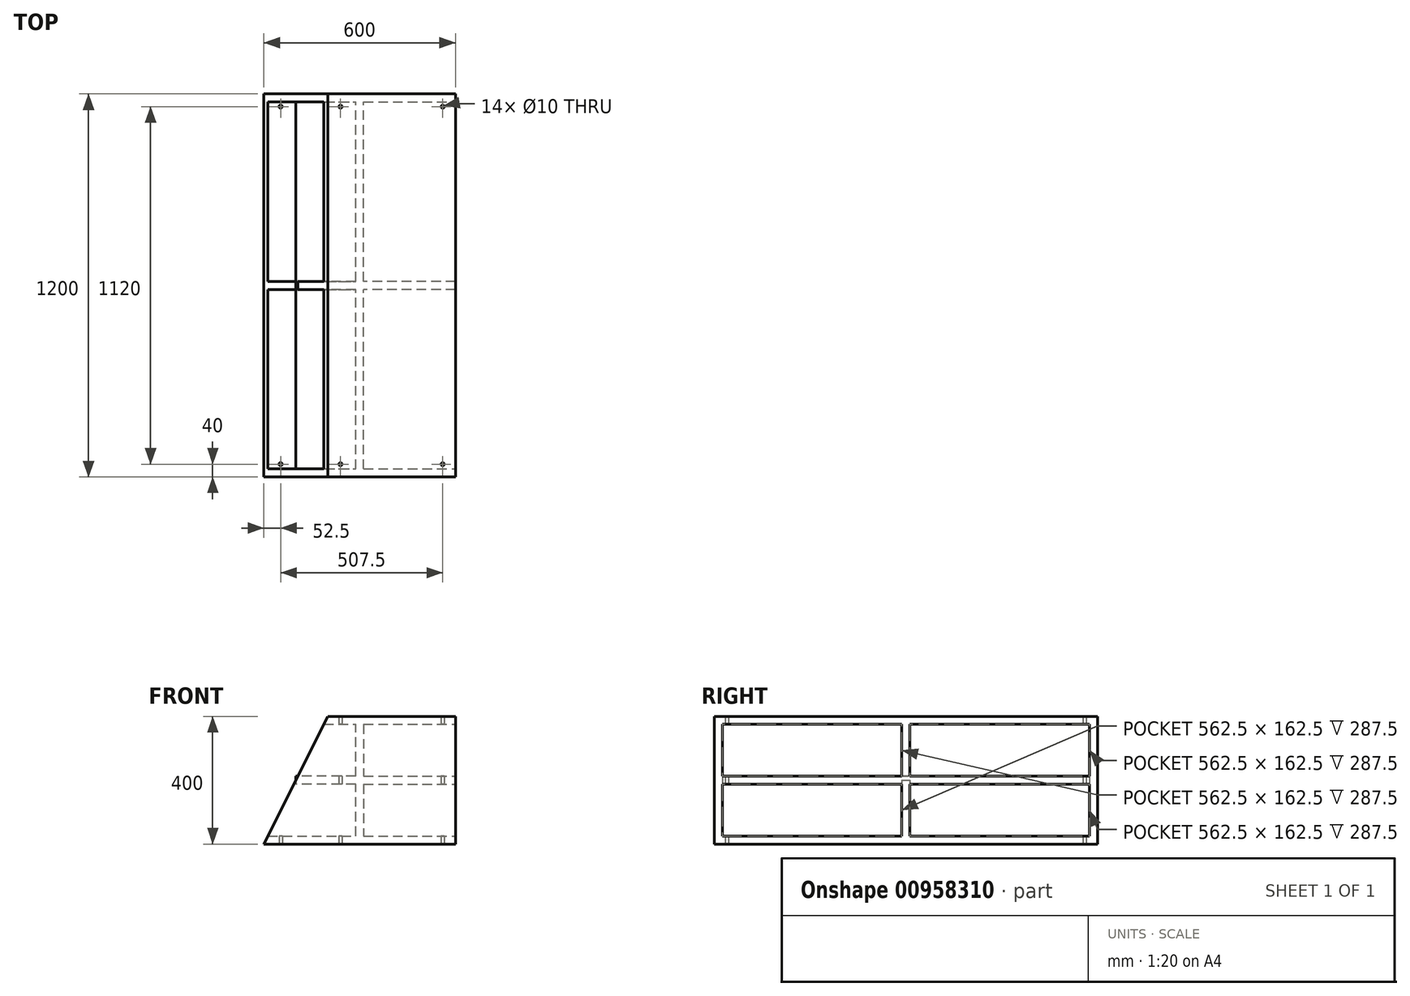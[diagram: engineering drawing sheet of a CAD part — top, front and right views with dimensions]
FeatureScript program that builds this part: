
annotation { "Feature Type Name" : "Feature", "Feature Type Description" : "" }
export const myFeature = defineFeature(function(context is Context, id is Id, definition is map)
    precondition{}
    {
        {
            var Q0;
            Q0=qCreatedBy(makeId("Front.planeOp"),FACE);
            var sketch = newSketch(context, id + "F0", { "sketchPlane" : qUnion([Q0])});
            skLineSegment(sketch, "E0.bottom", {"start": v(-400, 200) * mm, "end": v(0, 200) * mm});
            skLineSegment(sketch, "E0.top", {"start": v(-600, -200) * mm, "end": v(0, -200) * mm});
            skLineSegment(sketch, "E0.left", {"start": v(-400, 200) * mm, "end": v(-600, -200) * mm});
            skLineSegment(sketch, "E0.right", {"start": v(0, 200) * mm, "end": v(0, -200) * mm});
            skPoint(sketch, "E1", {"position": v(0, -200) * mm});
            skPoint(sketch, "E2", {"position": v(-500, 0) * mm});
            skSolve(sketch);
        }
        {
            var Q0;
            Q0=makeQuery(id+"F0.imprint","IMPRINT",FACE,{"disambiguationData":[TD([[makeQuery(id+"F0.imprint","IMPRINT",EDGE,{"derivedFrom":sQuery(id+"F0.wireOp",EDGE,"E0.bottom")}),-1.0]])]});
            extrude(context, id + "F1", {"entities" : qUnion([Q0]), "endBound" : BoundingType.SYMMETRIC, "depth" : 1200 * mm, "offsetDistance" : 25 * mm});
        }
        {
            var Q0;
            Q0=makeQuery(id+"F1.opExtrude","SWEPT_FACE",FACE,{"disambiguationData":[OSD([sQuery(id+"F0.wireOp",EDGE,"E0.right")])]});
            var Q1;
            Q1=makeQuery(id+"F1.opExtrude","SWEPT_FACE",FACE,{"disambiguationData":[OSD([sQuery(id+"F0.wireOp",EDGE,"E0.left")])]});
            shell(context, id + "F2", {"entities" : qUnion([Q0, Q1]), "thickness" : 25 * mm});
        }
        {
            var Q0;
            Q0=makeQuery(id+"F0.imprint","IMPRINT",FACE,{"disambiguationData":[TD([[makeQuery(id+"F0.imprint","IMPRINT",EDGE,{"derivedFrom":sQuery(id+"F0.wireOp",EDGE,"E0.bottom")}),-1.0]])]});
            extrude(context, id + "F3", {"entities" : qUnion([Q0]), "operationType" : NewBodyOperationType.ADD, "endBound" : BoundingType.SYMMETRIC, "depth" : 25 * mm, "offsetDistance" : 25 * mm});
        }
        {
            var Q0;
            Q0=qCreatedBy(makeId("Top.planeOp"),FACE);
            var sketch = newSketch(context, id + "F4", { "sketchPlane" : qUnion([Q0])});
            skLineSegment(sketch, "E3.bottom", {"start": v(-500, -575) * mm, "end": v(0, -575) * mm});
            skLineSegment(sketch, "E3.top", {"start": v(-500, 575) * mm, "end": v(0, 575) * mm});
            skLineSegment(sketch, "E3.left", {"start": v(-500, -575) * mm, "end": v(-500, 575) * mm});
            skLineSegment(sketch, "E3.right", {"start": v(0, -575) * mm, "end": v(0, 575) * mm});
            skSolve(sketch);
        }
        {
            var Q0;
            Q0 = qSketchRegion(id + "F4", true);
            extrude(context, id + "F5", {"entities" : qUnion([Q0]), "operationType" : NewBodyOperationType.ADD, "endBound" : BoundingType.SYMMETRIC, "depth" : 25 * mm, "offsetDistance" : 25 * mm});
        }
        {
            var Q0;
            Q0=qCreatedBy(makeId("Right.planeOp"),FACE);
            cPlane(context, id + "F6", {"entities" : qUnion([Q0]), "cplaneType" : CPlaneType.OFFSET, "offset" : 300 * mm, "oppositeDirection" : true, "width" : 150 * mm, "height" : 150 * mm});
        }
        {
            var Q0;
            Q0=qCreatedBy(id+"F6.planeOp",FACE);
            var sketch = newSketch(context, id + "F7", { "sketchPlane" : qUnion([Q0])});
            skLineSegment(sketch, "E4.bottom", {"start": v(-575, 175) * mm, "end": v(575, 175) * mm});
            skLineSegment(sketch, "E4.top", {"start": v(-575, -175) * mm, "end": v(575, -175) * mm});
            skLineSegment(sketch, "E4.left", {"start": v(-575, 175) * mm, "end": v(-575, -175) * mm});
            skLineSegment(sketch, "E4.right", {"start": v(575, 175) * mm, "end": v(575, -175) * mm});
            skSolve(sketch);
        }
        {
            var Q0;
            Q0=makeQuery(id+"F7.imprint","IMPRINT",FACE,{"disambiguationData":[TD([[makeQuery(id+"F7.imprint","IMPRINT",EDGE,{"derivedFrom":sQuery(id+"F7.wireOp",EDGE,"E4.bottom")}),-1.0]])]});
            extrude(context, id + "F8", {"entities" : qUnion([Q0]), "operationType" : NewBodyOperationType.ADD, "endBound" : BoundingType.SYMMETRIC, "depth" : 25 * mm, "offsetDistance" : 25 * mm});
        }
        {
            var Q0;
            Q0=makeQuery(id+"F1.opExtrude","SWEPT_FACE",FACE,{"disambiguationData":[OSD([sQuery(id+"F0.wireOp",EDGE,"E0.top")])]});
            var sketch = newSketch(context, id + "F9", { "sketchPlane" : qUnion([Q0])});
            skPoint(sketch, "E5", {"position": v(-40, 560) * mm});
            skPoint(sketch, "E6", {"position": v(-547.5, 560) * mm});
            skPoint(sketch, "E7", {"position": v(-40, -560) * mm});
            skPoint(sketch, "E8", {"position": v(-547.5, -560) * mm});
            skPoint(sketch, "E9", {"position": v(-360, 560) * mm});
            skPoint(sketch, "E10", {"position": v(-360, -560) * mm});
            skPoint(sketch, "E11", {"position": v(88.6, 881.31) * mm});
            skSolve(sketch);
        }
        {
            var Q0;
            Q0=sQuery(id+"F9.wireOp",VERTEX,"E5");
            var Q1;
            Q1=sQuery(id+"F9.wireOp",VERTEX,"E6");
            var Q2;
            Q2=sQuery(id+"F9.wireOp",VERTEX,"E7");
            var Q3;
            Q3=sQuery(id+"F9.wireOp",VERTEX,"E8");
            var Q4;
            Q4=sQuery(id+"F9.wireOp",VERTEX,"E9");
            var Q5;
            Q5=sQuery(id+"F9.wireOp",VERTEX,"E10");
            var Q6;
            Q6=makeQuery(id+"F1.opExtrude","SWEPT_BODY",BODY,{"disambiguationData":[OSD([sQuery(id+"F0.wireOp",EDGE,"E0.bottom"),sQuery(id+"F0.wireOp",EDGE,"E0.top"),sQuery(id+"F0.wireOp",EDGE,"E0.left"),sQuery(id+"F0.wireOp",EDGE,"E0.right")])]});
            hole(context, id + "F10", {"style" : HoleStyle.SIMPLE, "endStyle" : HoleEndStyle.THROUGH, "holeDiameter" : 10 * mm, "majorDiameter" : 5 * mm, "isTappedThrough" : true, "tappedDepth" : 12 * mm, "tapClearance" : 3, "locations" : qUnion([Q0, Q1, Q2, Q3, Q4, Q5]), "scope" : qUnion([Q6])});
        }
    });
